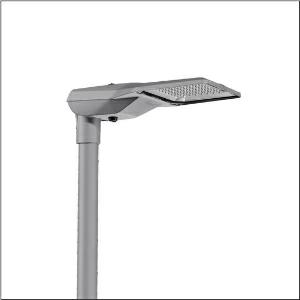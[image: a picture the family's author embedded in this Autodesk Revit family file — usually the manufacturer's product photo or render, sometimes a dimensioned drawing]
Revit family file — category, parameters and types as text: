
# Revit family: streetlight_sl_21_iq_midi___pc-l_5xe3f31y08mb_244c
name_source: partatom
category: Lighting Fixtures
units: mm (PartAtom-declared; Revit-internal decimal feet)

## family parameters
Cut with Voids When Loaded = No
Host = Face
Light Source = No
Part Type = Normal
Room Calculation Point = No
Round Connector Dimension = Use Diameter
Shared = No

## types (1)
- --- (1 x LED, 17070 lm, 129.3 W, 3000K)
    Apparent Load = 129 VA
    CIE Flux Codes = 38 78 98 100 100
    Color Rendering = 70
    Color Temperature = 3000K
    Default Elevation = 1800 mm
    Description = Streetlight SL 21 iQ midi, mast luminaire, primary light control with lens, of PMMA, primary optical cover: cover, of toughened safety glass, transparent, light distribution: PC-L, light emission: direct distribution, primary light characteristic: asymmetric, left, installation type: post-top, side-entry, LED, High Power LED, rated luminous flux: 17.070lm, luminous efficacy: 132lm/W, light colour: 730, colour temperature: 3000K, control: pre-setting: logarithmic dimming characteristic, Street-Remote, Auto-Match, Temp-Guard, Lumen-Switch, Night-Set, Smart-Wire, Light-Fading, Desk-Remote (wireless, voltage-free reading and setting of iQ features in the workshop via application-optimized NFC function/RFID function), optimised constant luminous flux control (CLO 2.0), mains connection: 230..240V, AC, 50/60Hz, start of lifetime: 129W, end of service life: 142W, reduction: 56W, luminaire housing, of diecast aluminium, powder-coated, Siteco® metallic grey (DB 702S), corrosivity category C5 mid according to DIN EN ISO 12944, please order mast flange separately, inclination adjustable: 0°, 5°, 10°, 15°, sealing non-destructively replaceable, multi-level sealing system, length: 644mm, width: 335mm, height: 110mm, mast flange for spigot size: 42mm (side-entry): 5XC10008XM4, 60/48mm (side-entry/post-top): 5XC10108XM2, 76/60mm (side-entry/post-top): 5XC10108XM1, Smart Interface below and above, protection rating (complete): IP66, insulation class (complete): insulation class II (safety insulation), certification: CE, ENEC, ENEC+, VDE, impact resistance: IK09, permissible operating ambient temperature for outdoor applications: -40..+50°C, standard-compliant lighting for roads and squares, packaging unit: 1 piece

Light Distribution: PC-L
    Height = 111 mm
    Lamp = 1 x LED
    Lamp Light Flux = 17070 lm
    Lamp Power = 129.3 W
    Lamp count = 1
    Length = 644 mm
    Luminous efficacy = 132 lm/W
    Manufacturer = Siteco
    ModVariant = No
    Model = 5XE3F31Y08MB
    Number of Poles = 1
    OnlyDefault = Yes
    Power Factor = 1
    Product Name = Streetlight SL 21 iQ midi | PC-L
    Product group = mast luminaire | pylon top
    ProductGroupID = 6100
    Protection Class = Protection class II
    Protection Degree = IP 66
    RLX_Detail_Level = 1
    RLX_Emergency_Light_Flux = 0 lm
    RLX_Emergency_Type = 0
    RLX_Emergency_Type_DB = No
    RlxData = <blob elided: 93337 chars, md5=9431ada8>
    Socket = socket
    Standby Power = 0 W
    System Light Flux = 17070 lm
    System Power = 129 W
    Type Comments = factory setting: luminous flux: 100 % | dim-lin: 254 | 672 mA
    Type Image = l_1004304.jpg
    URL = http://relux.com
    VarID = @adj_032725
    Voltage = 0 V
    Weight = 0.00 kg
    Width = 336 mm

## geometry (parser evidence)
native form markers: Blend x4, Sweep x9
no freeform markers — native parametric forms only
